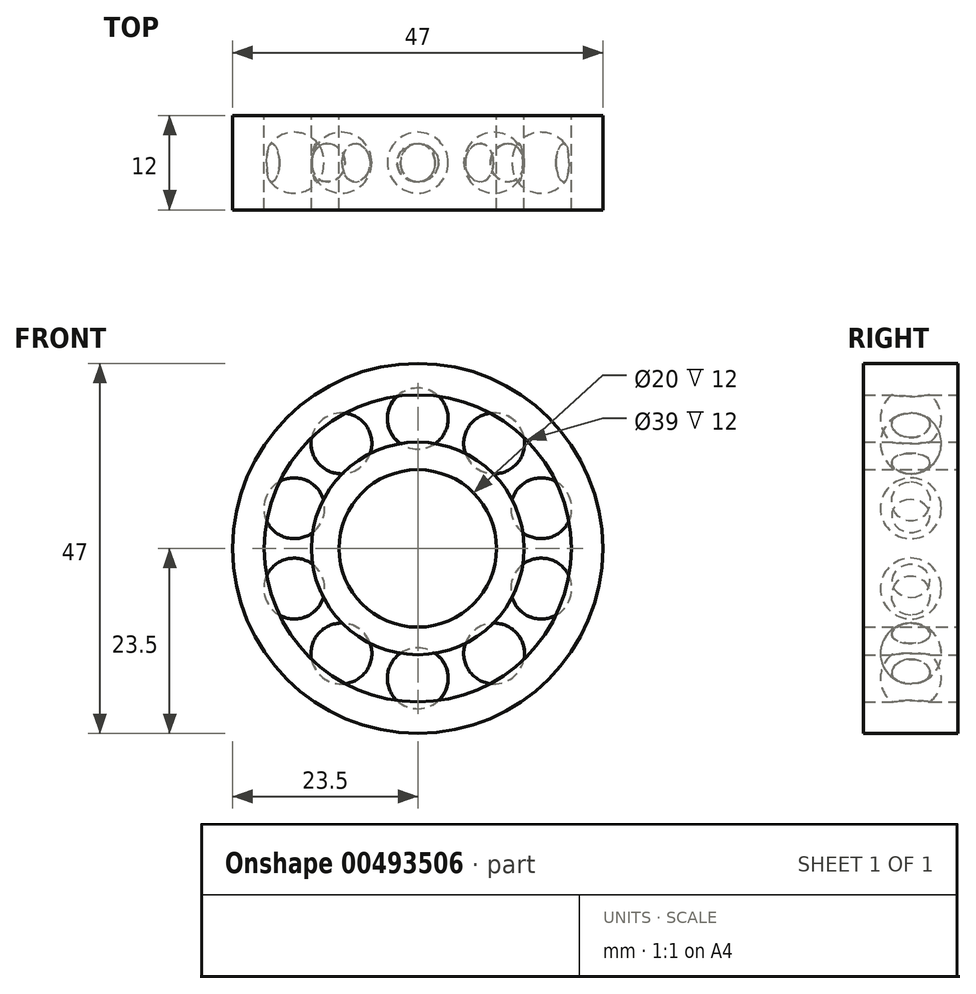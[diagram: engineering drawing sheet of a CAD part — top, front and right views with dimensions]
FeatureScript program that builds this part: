
annotation { "Feature Type Name" : "Feature", "Feature Type Description" : "" }
export const myFeature = defineFeature(function(context is Context, id is Id, definition is map)
    precondition{}
    {
        {
            var Q0;
            Q0=qCreatedBy(makeId("Front.planeOp"),FACE);
            var sketch = newSketch(context, id + "F0", { "sketchPlane" : qUnion([Q0])});
            skCircle(sketch, "E0", {"center": v(0, 0) * mm, "radius": 10 * mm});
            skCircle(sketch, "E1", {"center": v(0, 0) * mm, "radius": 13.5 * mm});
            skCircle(sketch, "E2", {"center": v(0, 0) * mm, "radius": 19.5 * mm});
            skCircle(sketch, "E3", {"center": v(0, 0) * mm, "radius": 23.5 * mm});
            skSolve(sketch);
        }
        {
            var Q0;
            Q0=makeQuery(id+"F0.imprint","IMPRINT",FACE,{"disambiguationData":[TD([[makeQuery(id+"F0.imprint","IMPRINT",EDGE,{"derivedFrom":sQuery(id+"F0.wireOp",EDGE,"E2")}),-1.0]])]});
            var Q1;
            Q1=makeQuery(id+"F0.imprint","IMPRINT",FACE,{"disambiguationData":[TD([[makeQuery(id+"F0.imprint","IMPRINT",EDGE,{"derivedFrom":sQuery(id+"F0.wireOp",EDGE,"E0")}),-1.0]])]});
            extrude(context, id + "F1", {"entities" : qUnion([Q0, Q1]), "endBound" : BoundingType.SYMMETRIC, "depth" : 12 * mm, "offsetDistance" : 25 * mm});
        }
        {
            var Q0;
            Q0=qCreatedBy(makeId("Front.planeOp"),FACE);
            var sketch = newSketch(context, id + "F2", { "sketchPlane" : qUnion([Q0])});
            skArc(sketch, "E4", {"start": v(0, 12.64) * mm, "mid": v(3.86, 16.5) * mm, "end": v(0, 20.36) * mm});
            skLineSegment(sketch, "E5", {"start": v(0, 20.36) * mm, "end": v(0, 12.64) * mm});
            skSolve(sketch);
        }
        {
            var Q0;
            Q0=makeQuery(id+"F2.imprint","IMPRINT",FACE,{"disambiguationData":[TD([[makeQuery(id+"F2.imprint","IMPRINT",EDGE,{"derivedFrom":sQuery(id+"F2.wireOp",EDGE,"E4")}),1.0]])]});
            var Q1;
            Q1=sQuery(id+"F2.wireOp",EDGE,"E5");
            revolve(context, id + "F3", {"entities" : qUnion([Q0]), "axis" : qUnion([Q1]), "revolveType" : RevolveType.FULL});
        }
        {
            var Q0;
            Q0=makeQuery(id+"F3.opRevolve","SWEPT_BODY",BODY,{"disambiguationData":[OSD([sQuery(id+"F2.wireOp",EDGE,"E4"),sQuery(id+"F2.wireOp",EDGE,"E5")])]});
            var Q1;
            Q1=makeQuery(id+"F1.opExtrude","CAP_EDGE",EDGE,{"disambiguationData":[OSD([sQuery(id+"F0.wireOp",EDGE,"E1")])],"isStart":false});
            circularPattern(context, id + "F4", {"operationType" : NewBodyOperationType.ADD, "entities" : qUnion([Q0]), "axis" : qUnion([Q1]), "angle" : 360 * degree, "instanceCount" : 10, "equalSpace" : true});
        }
    });
